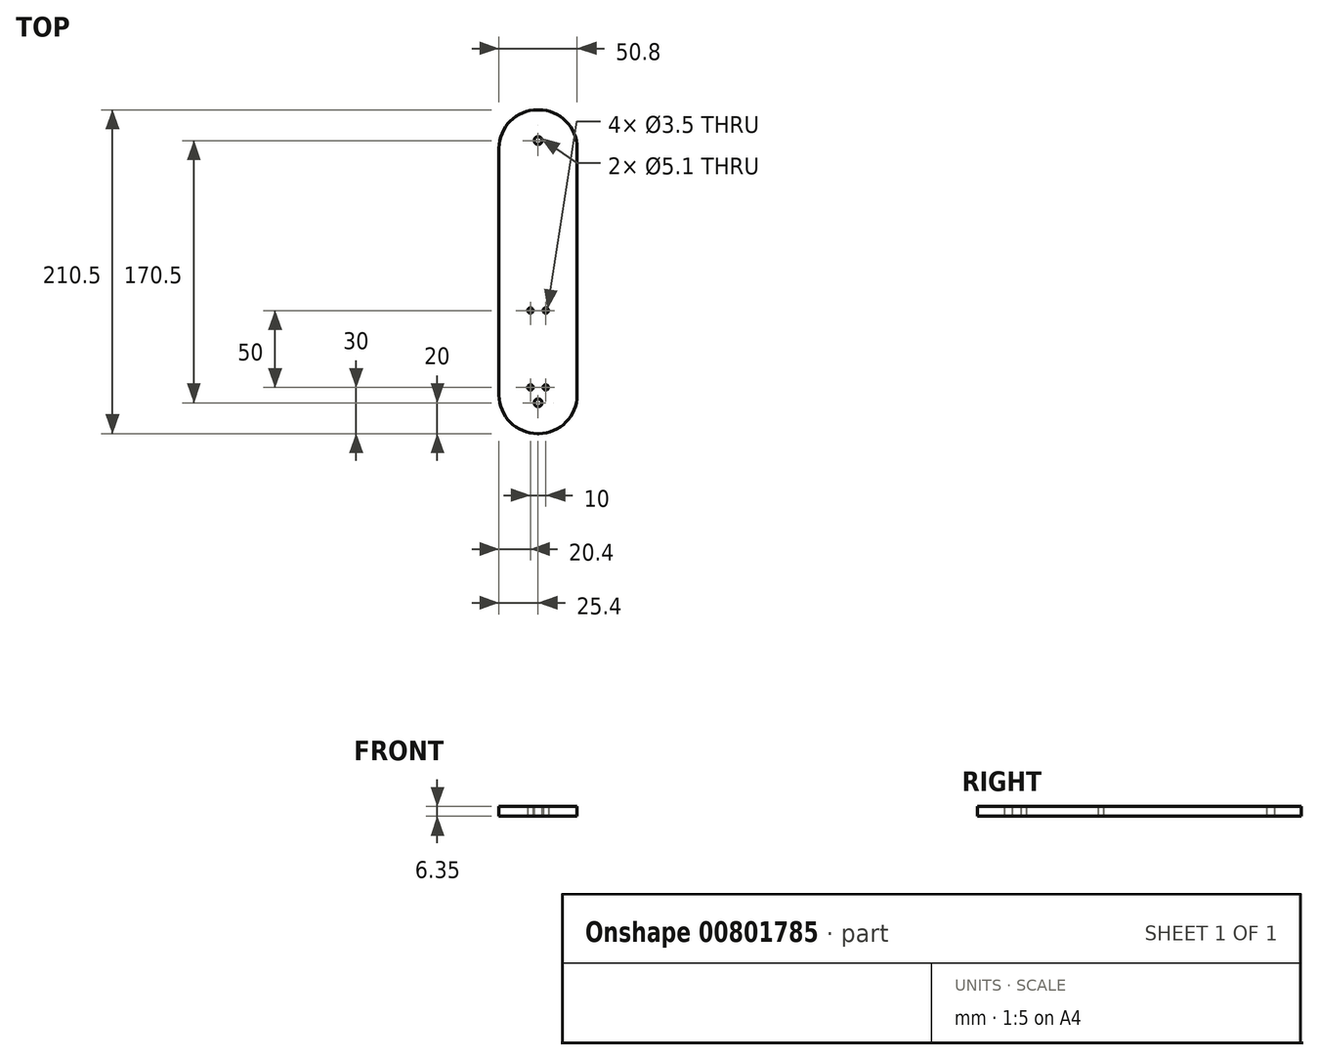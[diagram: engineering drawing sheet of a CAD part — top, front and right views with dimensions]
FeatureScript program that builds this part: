
annotation { "Feature Type Name" : "Feature", "Feature Type Description" : "" }
export const myFeature = defineFeature(function(context is Context, id is Id, definition is map)
    precondition{}
    {
        {
            var Q0;
            Q0=qCreatedBy(makeId("Top.planeOp"),FACE);
            var sketch = newSketch(context, id + "F0", { "sketchPlane" : qUnion([Q0])});
            skLineSegment(sketch, "E0.bottom", {"start": v(0.4, 105.25) * mm, "end": v(-0.4, 105.25) * mm});
            skLineSegment(sketch, "E0.top", {"start": v(0.4, -105.25) * mm, "end": v(-0.4, -105.25) * mm});
            skLineSegment(sketch, "E0.left", {"start": v(25.4, 80.25) * mm, "end": v(25.4, -80.25) * mm});
            skLineSegment(sketch, "E0.right", {"start": v(-25.4, 80.25) * mm, "end": v(-25.4, -80.25) * mm});
            skPoint(sketch, "E0.middle", {"position": v(0, 0) * mm});
            skCircle(sketch, "E1", {"center": v(0, 85.25) * mm, "radius": 2.55 * mm});
            skPoint(sketch, "E2.visualSharp", {"position": v(-25.4, -105.25) * mm});
            skArc(sketch, "E2.filletArc", {"start": v(-25.4, -80.25) * mm, "mid": v(-18.08, -97.93) * mm, "end": v(-0.4, -105.25) * mm});
            skPoint(sketch, "E3.visualSharp", {"position": v(25.4, -105.25) * mm});
            skArc(sketch, "E3.filletArc", {"start": v(0.4, -105.25) * mm, "mid": v(18.08, -97.93) * mm, "end": v(25.4, -80.25) * mm});
            skPoint(sketch, "E4.visualSharp", {"position": v(25.4, 105.25) * mm});
            skArc(sketch, "E4.filletArc", {"start": v(25.4, 80.25) * mm, "mid": v(18.08, 97.93) * mm, "end": v(0.4, 105.25) * mm});
            skPoint(sketch, "E5.visualSharp", {"position": v(-25.4, 105.25) * mm});
            skArc(sketch, "E5.filletArc", {"start": v(-0.4, 105.25) * mm, "mid": v(-18.08, 97.93) * mm, "end": v(-25.4, 80.25) * mm});
            skCircle(sketch, "E6.MirrorC", {"center": v(0, -85.25) * mm, "radius": 2.55 * mm});
            skCircle(sketch, "E7.MirrorC", {"center": v(5, -25.25) * mm, "radius": 1.75 * mm});
            skCircle(sketch, "E8.MirrorC", {"center": v(-5, -25.25) * mm, "radius": 1.75 * mm});
            skCircle(sketch, "E9.MirrorC", {"center": v(-5, -75.25) * mm, "radius": 1.75 * mm});
            skCircle(sketch, "E10.MirrorC", {"center": v(5, -75.25) * mm, "radius": 1.75 * mm});
            skLineSegment(sketch, "E11", {"start": v(-5, -25.25) * mm, "end": v(5, -25.25) * mm, "construction": true});
            skLineSegment(sketch, "E12", {"start": v(-5, -75.25) * mm, "end": v(5, -75.25) * mm, "construction": true});
            skSolve(sketch);
        }
        {
            var Q0;
            Q0=makeQuery(id+"F0.imprint","IMPRINT",FACE,{"disambiguationData":[TD([[makeQuery(id+"F0.imprint","IMPRINT",EDGE,{"derivedFrom":sQuery(id+"F0.wireOp",EDGE,"E0.bottom")}),1.0]])]});
            extrude(context, id + "F1", {"entities" : qUnion([Q0]), "depth" : 6.35 * mm, "offsetDistance" : 25 * mm});
        }
    });
